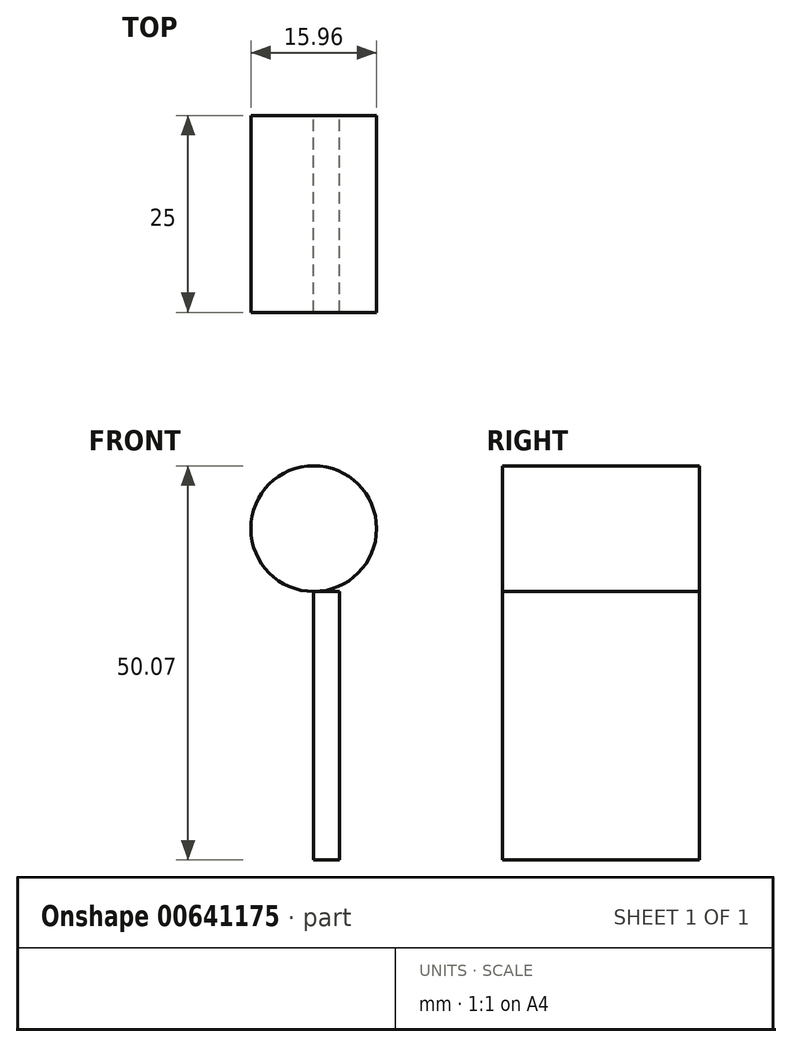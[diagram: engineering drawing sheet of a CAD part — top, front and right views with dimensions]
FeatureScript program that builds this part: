
annotation { "Feature Type Name" : "Feature", "Feature Type Description" : "" }
export const myFeature = defineFeature(function(context is Context, id is Id, definition is map)
    precondition{}
    {
        {
            var Q0;
            Q0=qCreatedBy(makeId("Front.planeOp"),FACE);
            var sketch = newSketch(context, id + "F0", { "sketchPlane" : qUnion([Q0])});
            skCircle(sketch, "E0", {"center": v(0, 0) * mm, "radius": 7.98 * mm});
            skLineSegment(sketch, "E1.bottom", {"start": v(0, -7.98) * mm, "end": v(3.28, -7.98) * mm});
            skLineSegment(sketch, "E1.top", {"start": v(0, -42.09) * mm, "end": v(3.28, -42.09) * mm});
            skLineSegment(sketch, "E1.left", {"start": v(0, -7.98) * mm, "end": v(0, -42.09) * mm});
            skLineSegment(sketch, "E1.right", {"start": v(3.28, -7.98) * mm, "end": v(3.28, -42.09) * mm});
            skLineSegment(sketch, "E2.MirrorCS", {"start": v(-3.28, -7.98) * mm, "end": v(-3.28, -42.09) * mm});
            skLineSegment(sketch, "E3.MirrorCS", {"start": v(0, -42.09) * mm, "end": v(-3.28, -42.09) * mm});
            skSolve(sketch);
        }
        {
            var Q0;
            Q0=makeQuery(id+"F0.imprint","IMPRINT",FACE,{"disambiguationData":[TD([[makeQuery(id+"F0.imprint","IMPRINT",EDGE,{"derivedFrom":sQuery(id+"F0.wireOp",EDGE,"E0")}),1.0]])]});
            var Q1;
            Q1=makeQuery(id+"F0.imprint","IMPRINT",FACE,{"disambiguationData":[TD([[makeQuery(id+"F0.imprint","IMPRINT",EDGE,{"derivedFrom":sQuery(id+"F0.wireOp",EDGE,"E1.bottom")}),-1.0]])]});
            extrude(context, id + "F1", {"entities" : qUnion([Q0, Q1]), "depth" : 25 * mm, "offsetDistance" : 25 * mm});
        }
    });
